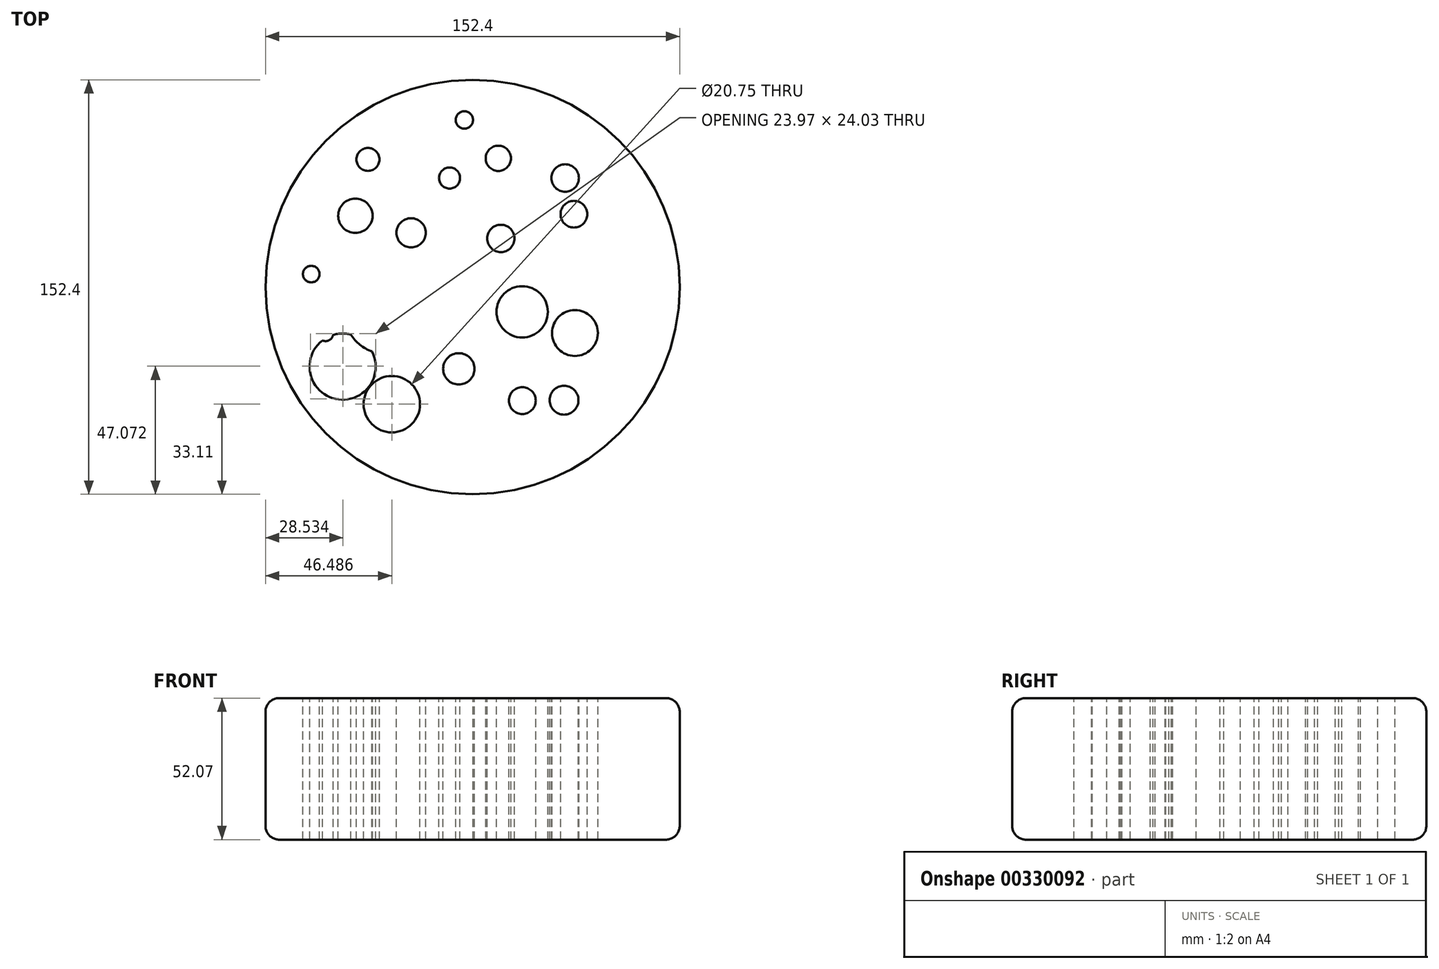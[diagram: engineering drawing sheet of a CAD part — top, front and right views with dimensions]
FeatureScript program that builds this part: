
annotation { "Feature Type Name" : "Feature", "Feature Type Description" : "" }
export const myFeature = defineFeature(function(context is Context, id is Id, definition is map)
    precondition{}
    {
        {
            var Q0;
            Q0=qCreatedBy(makeId("Top.planeOp"),FACE);
            var sketch = newSketch(context, id + "F0", { "sketchPlane" : qUnion([Q0])});
            skCircle(sketch, "E0", {"center": v(0, 0) * mm, "radius": 76.2 * mm});
            skSolve(sketch);
        }
        {
            var Q0;
            Q0 = qSketchRegion(id + "F0", true);
            extrude(context, id + "F1", {"entities" : qUnion([Q0]), "depth" : 52.07 * mm});
        }
        {
            var Q0;
            Q0=makeQuery(id+"F1.opExtrude","CAP_EDGE",EDGE,{"disambiguationData":[OSD([sQuery(id+"F0.wireOp",EDGE,"E0")])],"isStart":true});
            var Q1;
            Q1=makeQuery(id+"F1.opExtrude","CAP_EDGE",EDGE,{"disambiguationData":[OSD([sQuery(id+"F0.wireOp",EDGE,"E0")])],"isStart":false});
            fillet(context, id + "F2", {"entities" : qUnion([Q0, Q1]), "radius" : 5.08 * mm, "tangentPropagation" : true, "allowEdgeOverflow" : false});
        }
        {
            var Q0;
            Q0=makeQuery(id+"F1.opExtrude","CAP_FACE",FACE,{"disambiguationData":[OSD([sQuery(id+"F0.wireOp",EDGE,"E0")])],"isStart":false});
            var sketch = newSketch(context, id + "F3", { "sketchPlane" : qUnion([Q0])});
            skCircle(sketch, "E1", {"center": v(-38.5, 46.96) * mm, "radius": 4.24 * mm});
            skCircle(sketch, "E2", {"center": v(-8.46, 40.1) * mm, "radius": 3.88 * mm});
            skCircle(sketch, "E3", {"center": v(9.47, 47.36) * mm, "radius": 4.65 * mm});
            skCircle(sketch, "E4", {"center": v(-3.02, 61.47) * mm, "radius": 3.19 * mm});
            skCircle(sketch, "E5", {"center": v(34.06, 40.1) * mm, "radius": 5.05 * mm});
            skCircle(sketch, "E6", {"center": v(37.28, 26.8) * mm, "radius": 4.9 * mm});
            skCircle(sketch, "E7", {"center": v(-43.12, 26.23) * mm, "radius": 6.31 * mm});
            skCircle(sketch, "E8", {"center": v(-22.62, 19.96) * mm, "radius": 5.37 * mm});
            skCircle(sketch, "E9", {"center": v(10.4, 17.88) * mm, "radius": 5.03 * mm});
            skCircle(sketch, "E10", {"center": v(18.26, -9.12) * mm, "radius": 9.43 * mm});
            skCircle(sketch, "E11", {"center": v(37.66, -16.92) * mm, "radius": 8.44 * mm});
            skCircle(sketch, "E12", {"center": v(-30.63, -19.13) * mm, "radius": 2.6 * mm});
            skCircle(sketch, "E13", {"center": v(-32.38, -9.87) * mm, "radius": 14.54 * mm});
            skCircle(sketch, "E14", {"center": v(-59.35, 4.77) * mm, "radius": 3.06 * mm});
            skCircle(sketch, "E15", {"center": v(-54.14, -17) * mm, "radius": 2.9 * mm});
            skCircle(sketch, "E16", {"center": v(-47.8, -29.27) * mm, "radius": 12.16 * mm});
            skCircle(sketch, "E17", {"center": v(-29.71, -43.09) * mm, "radius": 10.37 * mm});
            skCircle(sketch, "E18", {"center": v(-5.06, -30.09) * mm, "radius": 5.76 * mm});
            skCircle(sketch, "E19", {"center": v(18.3, -41.76) * mm, "radius": 4.94 * mm});
            skCircle(sketch, "E20", {"center": v(33.64, -41.62) * mm, "radius": 5.32 * mm});
            skSolve(sketch);
        }
        {
            var Q0;
            {var subQ0=sQuery(id+"F3.wireOp",EDGE,"E16");var subQ1=sQuery(id+"F3.wireOp",EDGE,"E13");var subQ2=makeQuery(id+"F3.imprint","INTERSECT",VERTEX,{"disambiguationData":[OD(0.0)],"derivedFrom":[subQ1,subQ0]});Q0=makeQuery(id+"F3.imprint","IMPRINT",FACE,{"disambiguationData":[TD([[makeQuery(id+"F3.imprint","IMPRINT",EDGE,{"disambiguationData":[TD([[subQ2,-1.0]])],"derivedFrom":subQ1}),-1.0]])]});}
            var Q1;
            Q1=makeQuery(id+"F3.imprint","IMPRINT",FACE,{"disambiguationData":[TD([[makeQuery(id+"F3.imprint","IMPRINT",EDGE,{"derivedFrom":sQuery(id+"F3.wireOp",EDGE,"E8")}),1.0]])]});
            var Q2;
            Q2=makeQuery(id+"F3.imprint","IMPRINT",FACE,{"disambiguationData":[TD([[makeQuery(id+"F3.imprint","IMPRINT",EDGE,{"derivedFrom":sQuery(id+"F3.wireOp",EDGE,"E1")}),1.0]])]});
            var Q3;
            Q3=makeQuery(id+"F3.imprint","IMPRINT",FACE,{"disambiguationData":[TD([[makeQuery(id+"F3.imprint","IMPRINT",EDGE,{"derivedFrom":sQuery(id+"F3.wireOp",EDGE,"E7")}),1.0]])]});
            var Q4;
            Q4=makeQuery(id+"F3.imprint","IMPRINT",FACE,{"disambiguationData":[TD([[makeQuery(id+"F3.imprint","IMPRINT",EDGE,{"derivedFrom":sQuery(id+"F3.wireOp",EDGE,"E2")}),1.0]])]});
            var Q5;
            Q5=makeQuery(id+"F3.imprint","IMPRINT",FACE,{"disambiguationData":[TD([[makeQuery(id+"F3.imprint","IMPRINT",EDGE,{"derivedFrom":sQuery(id+"F3.wireOp",EDGE,"E3")}),1.0]])]});
            var Q6;
            Q6=makeQuery(id+"F3.imprint","IMPRINT",FACE,{"disambiguationData":[TD([[makeQuery(id+"F3.imprint","IMPRINT",EDGE,{"derivedFrom":sQuery(id+"F3.wireOp",EDGE,"E4")}),1.0]])]});
            var Q7;
            Q7=makeQuery(id+"F3.imprint","IMPRINT",FACE,{"disambiguationData":[TD([[makeQuery(id+"F3.imprint","IMPRINT",EDGE,{"derivedFrom":sQuery(id+"F3.wireOp",EDGE,"E9")}),1.0]])]});
            var Q8;
            Q8=makeQuery(id+"F3.imprint","IMPRINT",FACE,{"disambiguationData":[TD([[makeQuery(id+"F3.imprint","IMPRINT",EDGE,{"derivedFrom":sQuery(id+"F3.wireOp",EDGE,"E6")}),1.0]])]});
            var Q9;
            Q9=makeQuery(id+"F3.imprint","IMPRINT",FACE,{"disambiguationData":[TD([[makeQuery(id+"F3.imprint","IMPRINT",EDGE,{"derivedFrom":sQuery(id+"F3.wireOp",EDGE,"E10")}),1.0]])]});
            var Q10;
            Q10=makeQuery(id+"F3.imprint","IMPRINT",FACE,{"disambiguationData":[TD([[makeQuery(id+"F3.imprint","IMPRINT",EDGE,{"derivedFrom":sQuery(id+"F3.wireOp",EDGE,"E11")}),1.0]])]});
            var Q11;
            Q11=makeQuery(id+"F3.imprint","IMPRINT",FACE,{"disambiguationData":[TD([[makeQuery(id+"F3.imprint","IMPRINT",EDGE,{"derivedFrom":sQuery(id+"F3.wireOp",EDGE,"E20")}),1.0]])]});
            var Q12;
            Q12=makeQuery(id+"F3.imprint","IMPRINT",FACE,{"disambiguationData":[TD([[makeQuery(id+"F3.imprint","IMPRINT",EDGE,{"derivedFrom":sQuery(id+"F3.wireOp",EDGE,"E19")}),1.0]])]});
            var Q13;
            Q13=makeQuery(id+"F3.imprint","IMPRINT",FACE,{"disambiguationData":[TD([[makeQuery(id+"F3.imprint","IMPRINT",EDGE,{"derivedFrom":sQuery(id+"F3.wireOp",EDGE,"E18")}),1.0]])]});
            var Q14;
            Q14=makeQuery(id+"F3.imprint","IMPRINT",FACE,{"disambiguationData":[TD([[makeQuery(id+"F3.imprint","IMPRINT",EDGE,{"derivedFrom":sQuery(id+"F3.wireOp",EDGE,"E17")}),1.0]])]});
            var Q15;
            Q15=makeQuery(id+"F3.imprint","IMPRINT",FACE,{"disambiguationData":[TD([[makeQuery(id+"F3.imprint","IMPRINT",EDGE,{"derivedFrom":sQuery(id+"F3.wireOp",EDGE,"E5")}),1.0]])]});
            var Q16;
            Q16=makeQuery(id+"F3.imprint","IMPRINT",FACE,{"disambiguationData":[TD([[makeQuery(id+"F3.imprint","IMPRINT",EDGE,{"derivedFrom":sQuery(id+"F3.wireOp",EDGE,"E14")}),1.0]])]});
            extrude(context, id + "F4", {"entities" : qUnion([Q0, Q1, Q2, Q3, Q4, Q5, Q6, Q7, Q8, Q9, Q10, Q11, Q12, Q13, Q14, Q15, Q16]), "operationType" : NewBodyOperationType.REMOVE, "endBound" : BoundingType.THROUGH_ALL, "oppositeDirection" : true, "depth" : 25.4 * mm});
        }
    });
